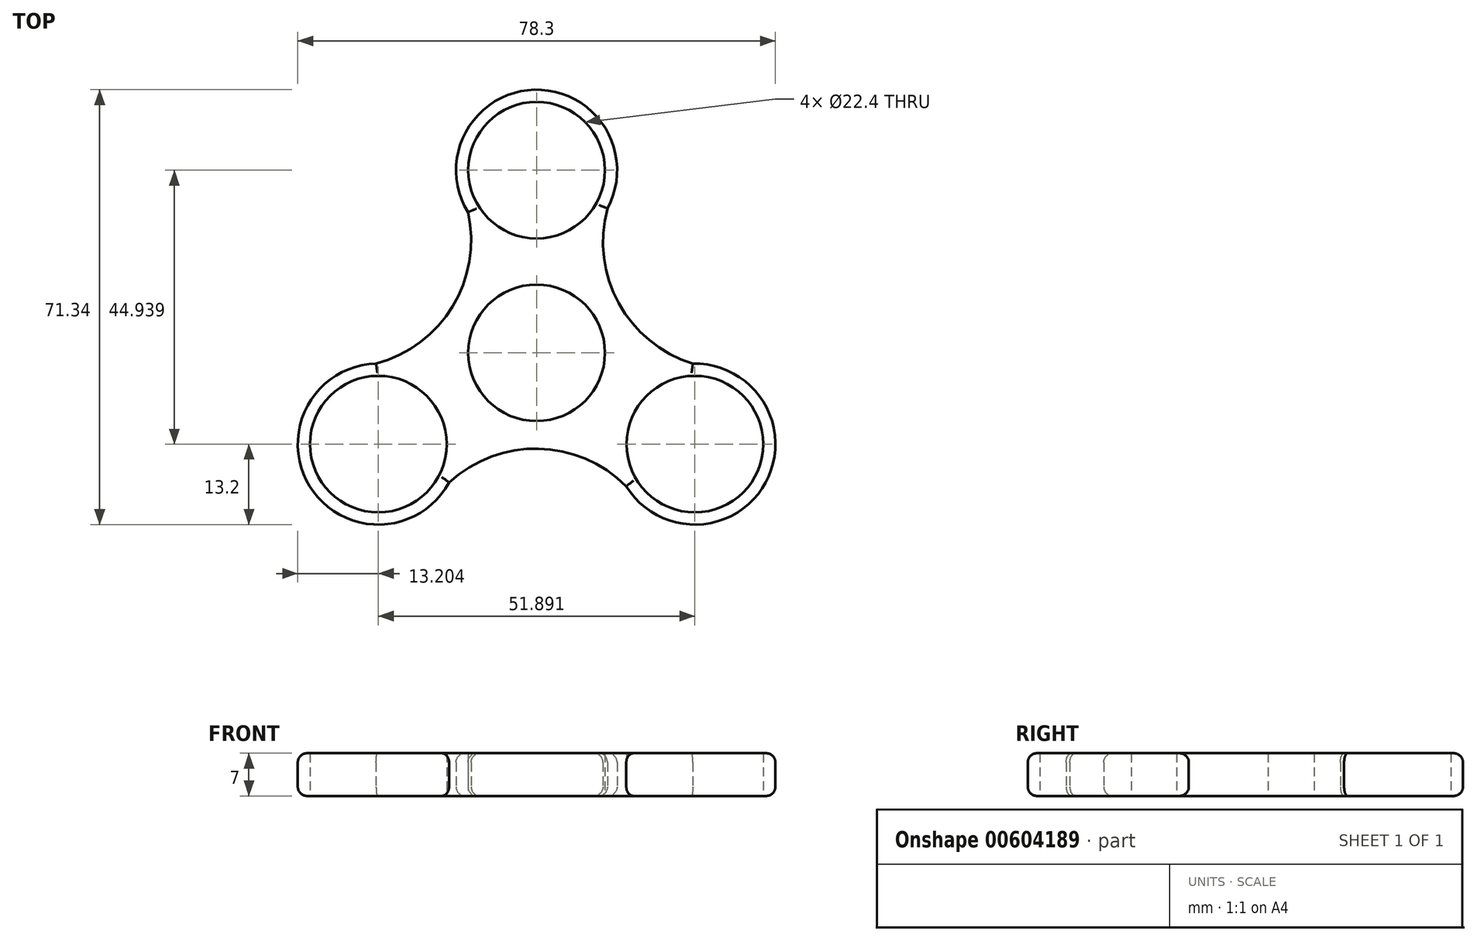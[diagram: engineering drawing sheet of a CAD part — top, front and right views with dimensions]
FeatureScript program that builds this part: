
annotation { "Feature Type Name" : "Feature", "Feature Type Description" : "" }
export const myFeature = defineFeature(function(context is Context, id is Id, definition is map)
    precondition{}
    {
        {
            var Q0;
            Q0=qCreatedBy(makeId("Top.planeOp"),FACE);
            var sketch = newSketch(context, id + "F0", { "sketchPlane" : qUnion([Q0])});
            skCircle(sketch, "E0", {"center": v(0, 0) * mm, "radius": 11.2 * mm});
            skCircle(sketch, "E1", {"center": v(0, 29.96) * mm, "radius": 11.2 * mm});
            skArc(sketch, "E2", {"start": v(11.61, 23.68) * mm, "mid": v(-0.35, 43.15) * mm, "end": v(-11.26, 23.07) * mm});
            skCircle(sketch, "E3.1.0", {"center": v(-25.95, -14.98) * mm, "radius": 11.2 * mm});
            skArc(sketch, "E3.1.1", {"start": v(-26.31, -1.78) * mm, "mid": v(-37.2, -21.88) * mm, "end": v(-14.35, -21.28) * mm});
            skCircle(sketch, "E3.2.0", {"center": v(25.95, -14.98) * mm, "radius": 11.2 * mm});
            skArc(sketch, "E3.2.1", {"start": v(14.7, -21.9) * mm, "mid": v(37.55, -21.27) * mm, "end": v(25.6, -1.78) * mm});
            skArc(sketch, "E4", {"start": v(11.61, 23.68) * mm, "mid": v(13.47, 8.12) * mm, "end": v(25.6, -1.78) * mm});
            skArc(sketch, "E5.1.0", {"start": v(-26.31, -1.78) * mm, "mid": v(-13.77, 7.6) * mm, "end": v(-11.26, 23.07) * mm});
            skArc(sketch, "E5.2.0", {"start": v(14.7, -21.9) * mm, "mid": v(0.3, -15.72) * mm, "end": v(-14.35, -21.28) * mm});
            skSolve(sketch);
        }
        {
            var Q0;
            Q0=makeQuery(id+"F0.imprint","IMPRINT",FACE,{"disambiguationData":[TD([[makeQuery(id+"F0.imprint","IMPRINT",EDGE,{"derivedFrom":sQuery(id+"F0.wireOp",EDGE,"E0")}),-1.0]])]});
            extrude(context, id + "F1", {"entities" : qUnion([Q0]), "depth" : 7 * mm, "offsetDistance" : 25 * mm});
        }
        {
            var Q0;
            Q0=makeQuery(id+"F1.opExtrude","CAP_EDGE",EDGE,{"disambiguationData":[OSD([sQuery(id+"F0.wireOp",EDGE,"E5.2.0")])],"isStart":false});
            var Q1;
            Q1=makeQuery(id+"F1.opExtrude","CAP_EDGE",EDGE,{"disambiguationData":[OSD([sQuery(id+"F0.wireOp",EDGE,"E5.2.0")])],"isStart":true});
            var Q2;
            Q2=makeQuery(id+"F1.opExtrude","CAP_EDGE",EDGE,{"disambiguationData":[OSD([sQuery(id+"F0.wireOp",EDGE,"E3.1.1")])],"isStart":false});
            var Q3;
            Q3=makeQuery(id+"F1.opExtrude","CAP_EDGE",EDGE,{"disambiguationData":[OSD([sQuery(id+"F0.wireOp",EDGE,"E5.1.0")])],"isStart":false});
            var Q4;
            Q4=makeQuery(id+"F1.opExtrude","CAP_EDGE",EDGE,{"disambiguationData":[OSD([sQuery(id+"F0.wireOp",EDGE,"E2")])],"isStart":false});
            var Q5;
            Q5=makeQuery(id+"F1.opExtrude","CAP_EDGE",EDGE,{"disambiguationData":[OSD([sQuery(id+"F0.wireOp",EDGE,"E4")])],"isStart":false});
            var Q6;
            Q6=makeQuery(id+"F1.opExtrude","CAP_EDGE",EDGE,{"disambiguationData":[OSD([sQuery(id+"F0.wireOp",EDGE,"E3.2.1")])],"isStart":false});
            fillet(context, id + "F2", {"entities" : qUnion([Q0, Q1, Q2, Q3, Q4, Q5, Q6]), "radius" : 1.5 * mm, "tangentPropagation" : true, "allowEdgeOverflow" : false});
        }
        {
            var Q0;
            Q0=makeQuery(id+"F1.opExtrude","CAP_EDGE",EDGE,{"disambiguationData":[OSD([sQuery(id+"F0.wireOp",EDGE,"E3.1.1")])],"isStart":true});
            var Q1;
            Q1=makeQuery(id+"F1.opExtrude","CAP_EDGE",EDGE,{"disambiguationData":[OSD([sQuery(id+"F0.wireOp",EDGE,"E5.1.0")])],"isStart":true});
            var Q2;
            Q2=makeQuery(id+"F1.opExtrude","CAP_EDGE",EDGE,{"disambiguationData":[OSD([sQuery(id+"F0.wireOp",EDGE,"E3.2.1")])],"isStart":true});
            var Q3;
            Q3=makeQuery(id+"F1.opExtrude","CAP_EDGE",EDGE,{"disambiguationData":[OSD([sQuery(id+"F0.wireOp",EDGE,"E4")])],"isStart":true});
            var Q4;
            Q4=makeQuery(id+"F1.opExtrude","CAP_EDGE",EDGE,{"disambiguationData":[OSD([sQuery(id+"F0.wireOp",EDGE,"E2")])],"isStart":true});
            fillet(context, id + "F3", {"entities" : qUnion([Q0, Q1, Q2, Q3, Q4]), "radius" : 1.5 * mm, "tangentPropagation" : true, "allowEdgeOverflow" : false});
        }
    });
